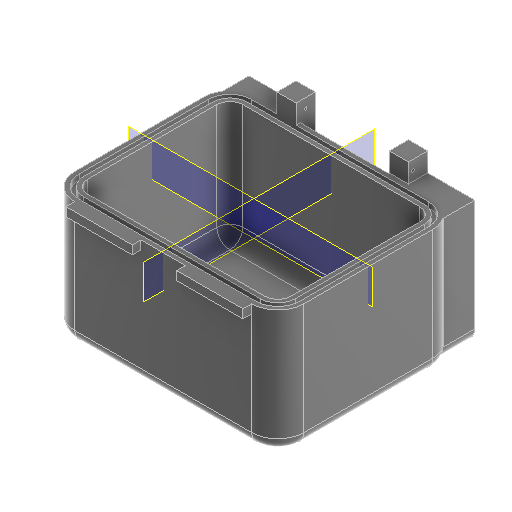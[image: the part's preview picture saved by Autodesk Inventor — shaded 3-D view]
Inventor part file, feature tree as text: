
AUTODESK INVENTOR PART (.ipt)
format: ipt  version: 2024.1 (Build 281209000, 209)  size: 2,394,624 bytes
history: native  units: mm
features: extrude x6, sketch x6, projected_geometry x5, plane x2, fillet x1, other x1
ambient origin geometry x8: Origin, YZ Plane, XZ Plane, XY Plane, X Axis, Y Axis, Z Axis, Center Point
bodies: Volumenkörper1 (feature_tree)
feature tree (21):
  extrude  "Extrusion1"  Depth=178.0mm
  extrude  "Extrusion2"  Depth=15.0mm
  fillet  "Rundung1"  Radius=137.0mm
  extrude  "Extrusion3"  Depth=15.0mm
  extrude  "Extrusion4"  Depth=5.0mm
  plane  "Arbeitsebene1"
  plane  "Arbeitsebene2"
  extrude  "Extrusion5"  Depth=5.0mm
  extrude  "Extrusion6"  Depth=76.0mm
  sketch  "Skizze1"  dims[d10=233.0mm d11=178.0mm]
  other  "Bild1"
  sketch  "Skizze2"  dims[d13=15.0mm d14=15.0mm d15=137.0mm d16=0.0mm]
  projected_geometry  "Projizierte Kontur1"
  sketch  "Skizze3"  dims[d17=6.0mm d18=0.0mm d19=15.0mm]
  projected_geometry  "Projizierte Kontur2"
  sketch  "Skizze4"  dims[d20=5.0mm d21=5.0mm]
  projected_geometry  "Projizierte Kontur3"
  sketch  "Skizze5"  dims[d22=6.0mm d23=0.0mm d24=5.0mm]
  projected_geometry  "Projizierte Kontur4"
  sketch  "Skizze6"  dims[d25=17.0mm d26=76.0mm d27=5.0mm d28=76.0mm d30=76.0mm d31=10.0mm d32=76.0mm d33=10.0mm d34=0.0mm d36=22.0mm d37=22.0mm d38=22.0mm d39=22.0mm d40=0.0mm d41=3.0mm d42=0.0mm d43=0.0mm]
  projected_geometry  "Projizierte Kontur5"
